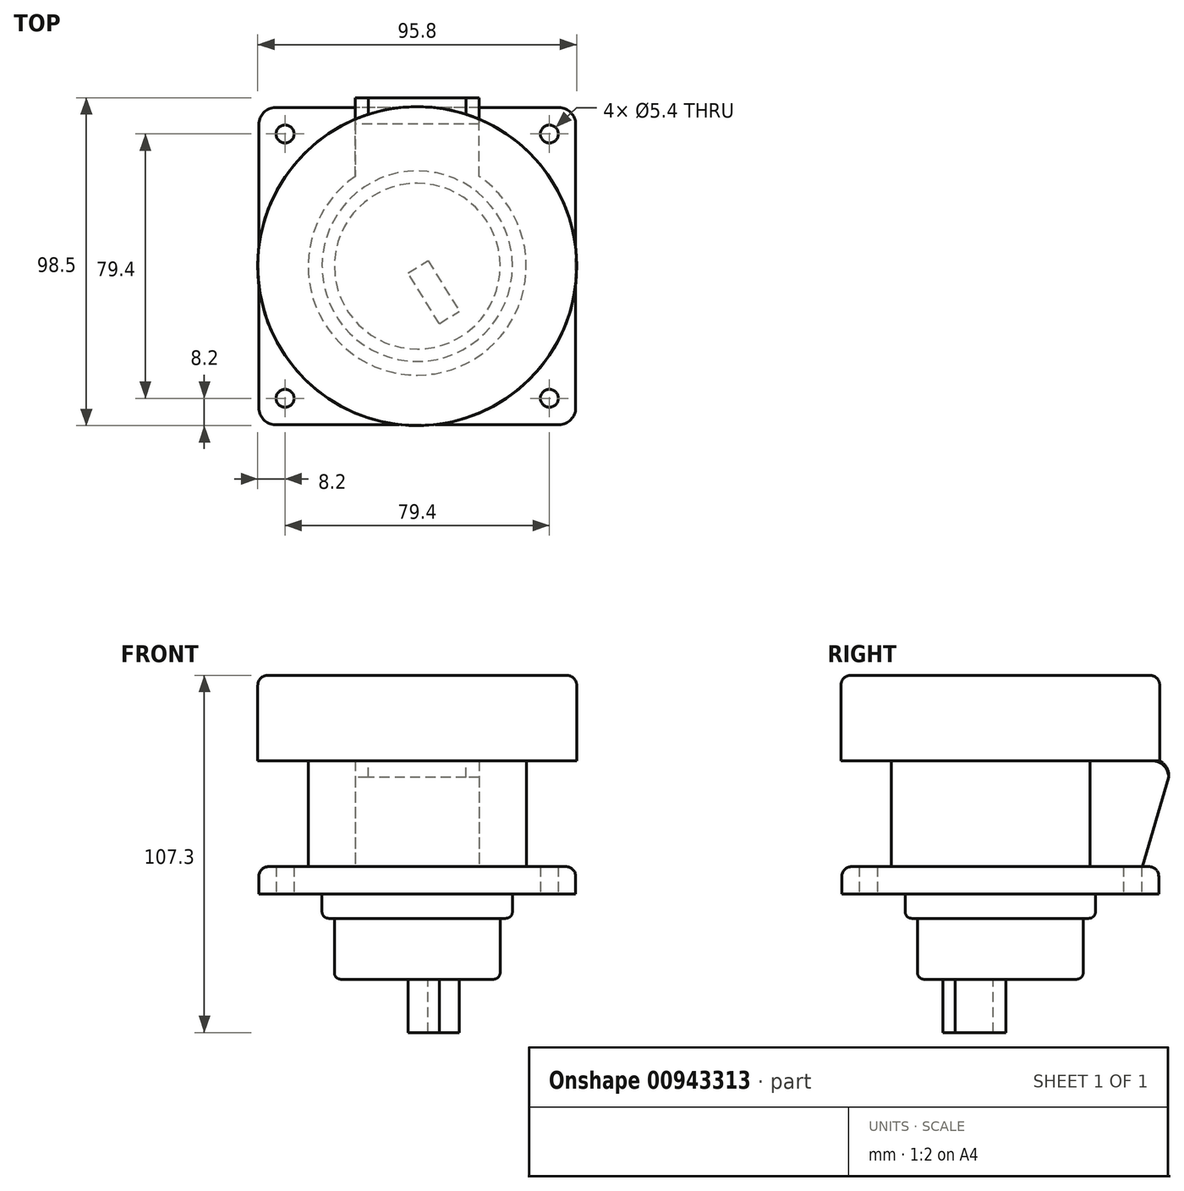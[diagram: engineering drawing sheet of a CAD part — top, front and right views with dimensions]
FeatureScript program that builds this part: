
annotation { "Feature Type Name" : "Feature", "Feature Type Description" : "" }
export const myFeature = defineFeature(function(context is Context, id is Id, definition is map)
    precondition{}
    {
        {
            var Q0;
            Q0=qCreatedBy(makeId("Top.planeOp"),FACE);
            var sketch = newSketch(context, id + "F0", { "sketchPlane" : qUnion([Q0])});
            skLineSegment(sketch, "E0.bottom", {"start": v(47.6, -47.6) * mm, "end": v(-47.6, -47.6) * mm});
            skLineSegment(sketch, "E0.top", {"start": v(47.6, 47.6) * mm, "end": v(-47.6, 47.6) * mm});
            skLineSegment(sketch, "E0.left", {"start": v(47.6, -47.6) * mm, "end": v(47.6, 47.6) * mm});
            skLineSegment(sketch, "E0.right", {"start": v(-47.6, -47.6) * mm, "end": v(-47.6, 47.6) * mm});
            skPoint(sketch, "E0.middle", {"position": v(0, 0) * mm});
            skCircle(sketch, "E1", {"center": v(-39.7, 39.7) * mm, "radius": 2.7 * mm});
            skCircle(sketch, "E2", {"center": v(39.7, 39.7) * mm, "radius": 2.7 * mm});
            skCircle(sketch, "E3.MirrorC", {"center": v(-39.7, -39.7) * mm, "radius": 2.7 * mm});
            skCircle(sketch, "E4.MirrorC", {"center": v(39.7, -39.7) * mm, "radius": 2.7 * mm});
            skCircle(sketch, "E5", {"center": v(0, 0) * mm, "radius": 32.75 * mm});
            skLineSegment(sketch, "E6.top", {"start": v(18.6, 50.6) * mm, "end": v(-18.6, 50.6) * mm});
            skLineSegment(sketch, "E6.left", {"start": v(18.6, 29.6) * mm, "end": v(18.6, 50.6) * mm});
            skLineSegment(sketch, "E6.right", {"start": v(-18.6, 29.6) * mm, "end": v(-18.6, 50.6) * mm});
            skPoint(sketch, "E6.middle", {"position": v(0, 40.1) * mm});
            skLineSegment(sketch, "E7", {"start": v(-18.6, 29.6) * mm, "end": v(-18.6, 26.96) * mm});
            skLineSegment(sketch, "E8", {"start": v(18.6, 29.6) * mm, "end": v(18.6, 26.96) * mm});
            skSolve(sketch);
        }
        {
            var Q0;
            Q0=makeQuery(id+"F0.imprint","IMPRINT",FACE,{"disambiguationData":[TD([[makeQuery(id+"F0.imprint","IMPRINT",EDGE,{"derivedFrom":sQuery(id+"F0.wireOp",EDGE,"E0.bottom")}),-1.0]])]});
            extrude(context, id + "F1", {"entities" : qUnion([Q0]), "depth" : 8.25 * mm, "offsetDistance" : 25 * mm});
        }
        {
            var Q0;
            {var subQ5=sQuery(id+"F0.wireOp",EDGE,"E6.top");Q0=makeQuery(id+"F0.imprint","IMPRINT",FACE,{"disambiguationData":[TD([[makeQuery(id+"F0.imprint","IMPRINT",EDGE,{"derivedFrom":subQ5}),1.0]])]});}
            var Q1;
            {var subQ6=sQuery(id+"F0.wireOp",EDGE,"E7");Q1=makeQuery(id+"F0.imprint","IMPRINT",FACE,{"disambiguationData":[TD([[makeQuery(id+"F0.imprint","IMPRINT",EDGE,{"derivedFrom":subQ6}),1.0]])]});}
            var Q2;
            {var subQ0=sQuery(id+"F0.wireOp",EDGE,"E5");var subQ1=makeQuery(id+"F0.imprint","INTERSECT",VERTEX,{"derivedFrom":[subQ0,sQuery(id+"F0.wireOp",EDGE,"E7")]});Q2=makeQuery(id+"F0.imprint","IMPRINT",FACE,{"disambiguationData":[TD([[makeQuery(id+"F0.imprint","IMPRINT",EDGE,{"disambiguationData":[TD([[subQ1,1.0]])],"derivedFrom":subQ0}),1.0]])]});}
            extrude(context, id + "F2", {"entities" : qUnion([Q0, Q1, Q2]), "operationType" : NewBodyOperationType.ADD, "depth" : 40 * mm, "offsetDistance" : 25 * mm});
        }
        {
            var Q0;
            Q0=makeQuery(id+"F2.opExtrude","CAP_FACE",FACE,{"disambiguationData":[OSD([sQuery(id+"F0.wireOp",EDGE,"E5"),sQuery(id+"F0.wireOp",EDGE,"E6.top"),sQuery(id+"F0.wireOp",EDGE,"E6.left"),sQuery(id+"F0.wireOp",EDGE,"E6.right"),sQuery(id+"F0.wireOp",EDGE,"E7"),sQuery(id+"F0.wireOp",EDGE,"E8")])],"isStart":false});
            var sketch = newSketch(context, id + "F3", { "sketchPlane" : qUnion([Q0])});
            skCircle(sketch, "E9", {"center": v(0, 0) * mm, "radius": 47.9 * mm});
            skSolve(sketch);
        }
        {
            var Q0;
            Q0 = qSketchRegion(id + "F3", true);
            extrude(context, id + "F4", {"entities" : qUnion([Q0]), "depth" : 25.7 * mm, "offsetDistance" : 25 * mm});
        }
        {
            var Q0;
            Q0=makeQuery(id+"F4.opExtrude","CAP_EDGE",EDGE,{"disambiguationData":[OSD([sQuery(id+"F3.wireOp",EDGE,"E9")])],"isStart":false});
            var Q1;
            Q1=makeQuery(id+"F1.opExtrude","CAP_EDGE",EDGE,{"disambiguationData":[OSD([sQuery(id+"F0.wireOp",EDGE,"E0.right")])],"isStart":false});
            var Q2;
            {var subQ0=sQuery(id+"F0.wireOp",EDGE,"E0.top");Q2=makeQuery(id+"F1.opExtrude","CAP_EDGE",EDGE,{"disambiguationData":[OSD([subQ0]),TDD([makeQuery(id+"F0.imprint","IMPRINT",EDGE,{"disambiguationData":[TD([[makeQuery(id+"F0.imprint","INTERSECT",VERTEX,{"derivedFrom":[subQ0,sQuery(id+"F0.wireOp",EDGE,"E0.right")]}),1.0]])],"derivedFrom":subQ0})])],"isStart":false});}
            var Q3;
            Q3=makeQuery(id+"F1.opExtrude","CAP_EDGE",EDGE,{"disambiguationData":[OSD([sQuery(id+"F0.wireOp",EDGE,"E0.bottom")])],"isStart":false});
            var Q4;
            Q4=makeQuery(id+"F1.opExtrude","CAP_EDGE",EDGE,{"disambiguationData":[OSD([sQuery(id+"F0.wireOp",EDGE,"E0.left")])],"isStart":false});
            var Q5;
            {var subQ0=sQuery(id+"F0.wireOp",EDGE,"E0.top");Q5=makeQuery(id+"F1.opExtrude","CAP_EDGE",EDGE,{"disambiguationData":[OSD([subQ0]),TDD([makeQuery(id+"F0.imprint","IMPRINT",EDGE,{"disambiguationData":[TD([[makeQuery(id+"F0.imprint","INTERSECT",VERTEX,{"derivedFrom":[subQ0,sQuery(id+"F0.wireOp",EDGE,"E0.left")]}),-1.0]])],"derivedFrom":subQ0})])],"isStart":false});}
            fillet(context, id + "F5", {"entities" : qUnion([Q0, Q1, Q2, Q3, Q4, Q5]), "radius" : 3 * mm, "tangentPropagation" : true, "allowEdgeOverflow" : false});
        }
        {
            var Q0;
            Q0=makeQuery(id+"F1.opExtrude","SWEPT_EDGE",EDGE,{"disambiguationData":[OSD([sQuery(id+"F0.wireOp",EDGE,"E0.bottom"),sQuery(id+"F0.wireOp",EDGE,"E0.right")])]});
            var Q1;
            Q1=makeQuery(id+"F1.opExtrude","SWEPT_EDGE",EDGE,{"disambiguationData":[OSD([sQuery(id+"F0.wireOp",EDGE,"E0.bottom"),sQuery(id+"F0.wireOp",EDGE,"E0.left")])]});
            var Q2;
            Q2=makeQuery(id+"F1.opExtrude","SWEPT_EDGE",EDGE,{"disambiguationData":[OSD([sQuery(id+"F0.wireOp",EDGE,"E0.top"),sQuery(id+"F0.wireOp",EDGE,"E0.left")])]});
            var Q3;
            Q3=makeQuery(id+"F1.opExtrude","SWEPT_EDGE",EDGE,{"disambiguationData":[OSD([sQuery(id+"F0.wireOp",EDGE,"E0.top"),sQuery(id+"F0.wireOp",EDGE,"E0.right")])]});
            var Q4;
            Q4=makeQuery(id+"F2.opExtrude","CAP_EDGE",EDGE,{"disambiguationData":[OSD([sQuery(id+"F0.wireOp",EDGE,"E6.top")])],"isStart":false});
            fillet(context, id + "F6", {"entities" : qUnion([Q0, Q1, Q2, Q3, Q4]), "radius" : 5 * mm, "tangentPropagation" : true, "allowEdgeOverflow" : false});
        }
        {
            var Q0;
            Q0=makeQuery(id+"F2.opExtrude","SWEPT_FACE",FACE,{"disambiguationData":[OSD([sQuery(id+"F0.wireOp",EDGE,"E6.right"),sQuery(id+"F0.wireOp",EDGE,"E7")])]});
            var sketch = newSketch(context, id + "F7", { "sketchPlane" : qUnion([Q0])});
            skLineSegment(sketch, "E10", {"start": v(-50.6, 35) * mm, "end": v(-42.64, 8.25) * mm});
            skSolve(sketch);
        }
        {
            var Q0;
            Q0 = qSketchRegion(id + "F7", true);
            var Q1;
            {var subQ4=sQuery(id+"F7.wireOp",EDGE,"E10");Q1=makeQuery(id+"F7.imprint","IMPRINT",FACE,{"disambiguationData":[TD([[makeQuery(id+"F7.imprint","IMPRINT",EDGE,{"derivedFrom":subQ4}),-1.0]])]});}
            extrude(context, id + "F8", {"entities" : qUnion([Q0, Q1]), "operationType" : NewBodyOperationType.REMOVE, "endBound" : BoundingType.THROUGH_ALL, "oppositeDirection" : true, "depth" : 25 * mm, "offsetDistance" : 25 * mm});
        }
        {
            var Q0;
            Q0=makeQuery(id+"F0.imprint","IMPRINT",FACE,{"disambiguationData":[TD([[makeQuery(id+"F0.imprint","IMPRINT",EDGE,{"derivedFrom":sQuery(id+"F0.wireOp",EDGE,"E0.bottom")}),-1.0]])]});
            var sketch = newSketch(context, id + "F9", { "sketchPlane" : qUnion([Q0])});
            skCircle(sketch, "E11", {"center": v(0, 0) * mm, "radius": 28.6 * mm});
            skCircle(sketch, "E12", {"center": v(0, 0) * mm, "radius": 24.9 * mm});
            skSolve(sketch);
        }
        {
            var Q0;
            Q0 = qSketchRegion(id + "F9", true);
            extrude(context, id + "F10", {"entities" : qUnion([Q0]), "operationType" : NewBodyOperationType.ADD, "oppositeDirection" : true, "depth" : 7.3 * mm, "offsetDistance" : 25 * mm});
        }
        {
            var Q0;
            Q0=makeQuery(id+"F9.imprint","IMPRINT",FACE,{"disambiguationData":[TD([[makeQuery(id+"F9.imprint","IMPRINT",EDGE,{"derivedFrom":sQuery(id+"F9.wireOp",EDGE,"E12")}),1.0]])]});
            extrude(context, id + "F11", {"entities" : qUnion([Q0]), "operationType" : NewBodyOperationType.ADD, "oppositeDirection" : true, "depth" : 25.6 * mm, "offsetDistance" : 25 * mm});
        }
        {
            var Q0;
            Q0=makeQuery(id+"F10.opExtrude","CAP_EDGE",EDGE,{"disambiguationData":[OSD([sQuery(id+"F9.wireOp",EDGE,"E11")])],"isStart":false});
            var Q1;
            Q1=makeQuery(id+"F11.opExtrude","CAP_EDGE",EDGE,{"disambiguationData":[OSD([sQuery(id+"F9.wireOp",EDGE,"E12")])],"isStart":false});
            fillet(context, id + "F12", {"entities" : qUnion([Q0, Q1]), "radius" : 2 * mm, "tangentPropagation" : true, "allowEdgeOverflow" : false});
        }
        {
            var Q0;
            Q0=makeQuery(id+"F11.opExtrude","CAP_FACE",FACE,{"disambiguationData":[OSD([sQuery(id+"F9.wireOp",EDGE,"E12")])],"isStart":false});
            var sketch = newSketch(context, id + "F13", { "sketchPlane" : qUnion([Q0])});
            skLineSegment(sketch, "E13", {"start": v(6.63, 17.26) * mm, "end": v(-2.78, 2.08) * mm});
            skLineSegment(sketch, "E14", {"start": v(-2.78, 2.08) * mm, "end": v(3.24, -1.65) * mm});
            skLineSegment(sketch, "E15", {"start": v(3.24, -1.65) * mm, "end": v(12.27, 12.93) * mm});
            skLineSegment(sketch, "E16", {"start": v(12.27, 12.93) * mm, "end": v(12.64, 13.53) * mm});
            skLineSegment(sketch, "E17", {"start": v(6.63, 17.26) * mm, "end": v(12.64, 13.53) * mm});
            skSolve(sketch);
        }
        {
            var Q0;
            Q0 = qSketchRegion(id + "F13", true);
            extrude(context, id + "F14", {"entities" : qUnion([Q0]), "operationType" : NewBodyOperationType.ADD, "depth" : 16 * mm, "offsetDistance" : 25 * mm});
        }
    });
